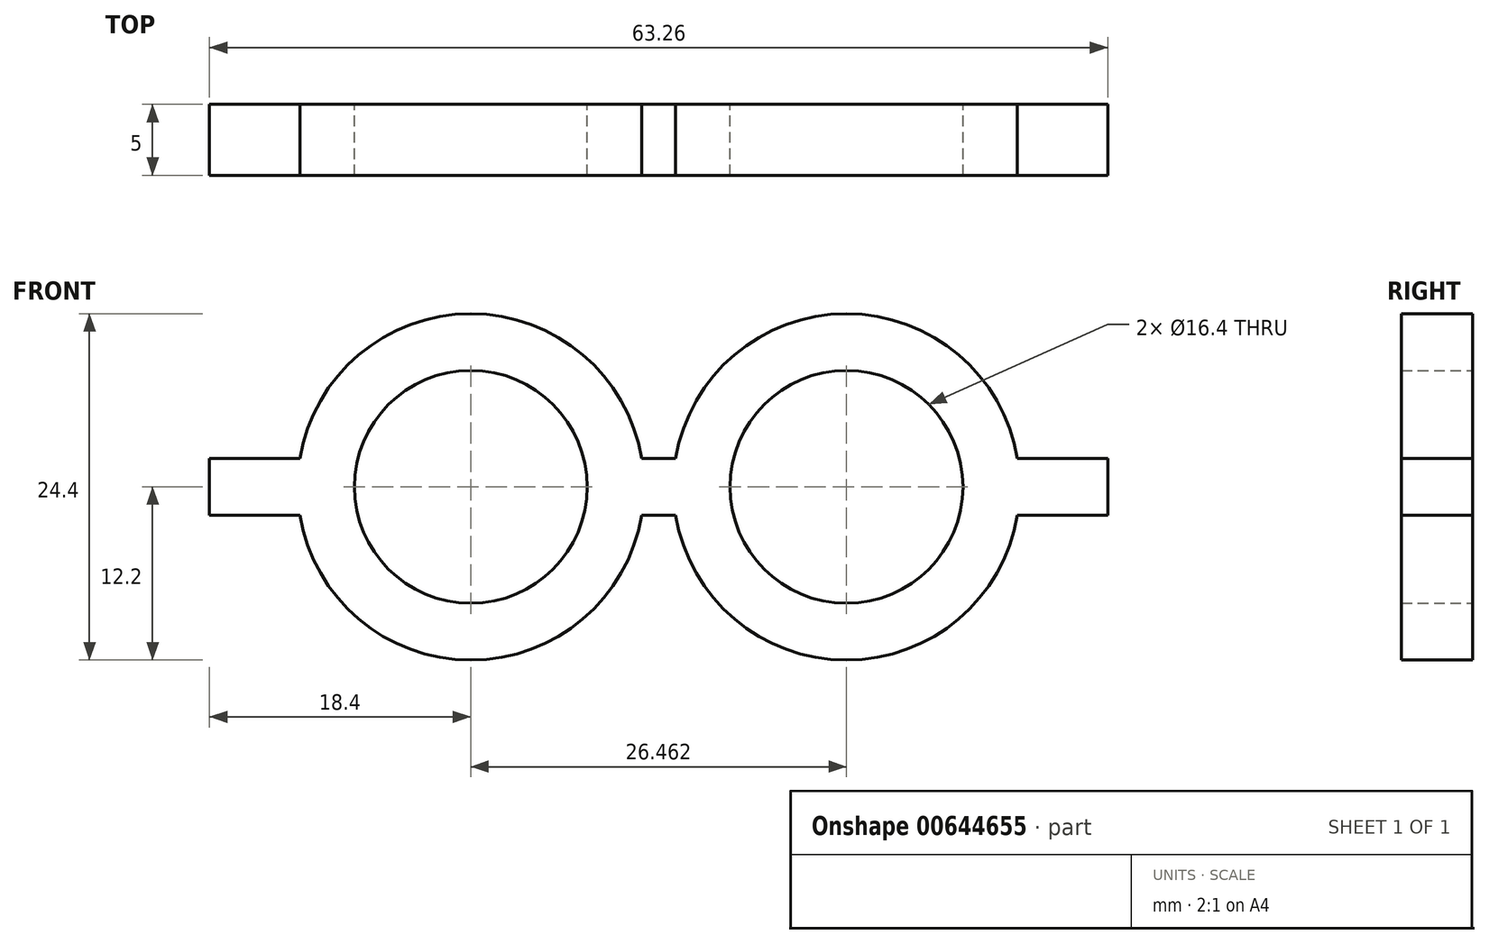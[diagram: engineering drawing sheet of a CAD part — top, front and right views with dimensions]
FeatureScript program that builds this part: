
annotation { "Feature Type Name" : "Feature", "Feature Type Description" : "" }
export const myFeature = defineFeature(function(context is Context, id is Id, definition is map)
    precondition{}
    {
        {
            var Q0;
            Q0=qCreatedBy(makeId("Front.planeOp"),FACE);
            var sketch = newSketch(context, id + "F0", { "sketchPlane" : qUnion([Q0])});
            skCircle(sketch, "E0", {"center": v(0, 0) * mm, "radius": 8.2 * mm});
            skArc(sketch, "E1.0", {"start": v(-12.03, -2) * mm, "mid": v(0, -12.2) * mm, "end": v(12.03, -2) * mm});
            skCircle(sketch, "E2.1.0.0", {"center": v(26.46, 0) * mm, "radius": 8.2 * mm});
            skArc(sketch, "E2.1.0.1", {"start": v(38.5, 2) * mm, "mid": v(26.46, 12.2) * mm, "end": v(14.43, 2) * mm});
            skLineSegment(sketch, "E2.direction1", {"start": v(0, 0) * mm, "end": v(26.46, 0) * mm, "construction": true});
            skLineSegment(sketch, "E3.bottom", {"start": v(14.43, -2) * mm, "end": v(12.03, -2) * mm});
            skLineSegment(sketch, "E3.top", {"start": v(14.43, 2) * mm, "end": v(12.03, 2) * mm});
            skPoint(sketch, "E3.middle", {"position": v(13.23, 0) * mm});
            skLineSegment(sketch, "E4.bottom", {"start": v(44.86, -2) * mm, "end": v(38.5, -2) * mm});
            skLineSegment(sketch, "E4.top", {"start": v(44.86, 2) * mm, "end": v(38.5, 2) * mm});
            skLineSegment(sketch, "E4.left", {"start": v(44.86, -2) * mm, "end": v(44.86, 2) * mm});
            skPoint(sketch, "E4.middle", {"position": v(35.66, 0) * mm});
            skLineSegment(sketch, "E5.right", {"start": v(-18.4, -2) * mm, "end": v(-18.4, 2) * mm});
            skPoint(sketch, "E5.middle", {"position": v(-9.2, 0) * mm});
            skPoint(sketch, "E6.orphan", {"position": v(26.46, 2) * mm});
            skPoint(sketch, "E4.right.start.orphan", {"position": v(26.46, -2) * mm});
            skLineSegment(sketch, "E7.trimOffspring", {"start": v(-12.03, 2) * mm, "end": v(-18.4, 2) * mm});
            skLineSegment(sketch, "E8.trimOffspring", {"start": v(-12.03, -2) * mm, "end": v(-18.4, -2) * mm});
            skPoint(sketch, "E9.orphan", {"position": v(0, 2) * mm});
            skPoint(sketch, "E5.left.start.orphan", {"position": v(0, -2) * mm});
            skArc(sketch, "E10.trimOffspring", {"start": v(12.03, 2) * mm, "mid": v(0, 12.2) * mm, "end": v(-12.03, 2) * mm});
            skArc(sketch, "E11.trimOffspring", {"start": v(14.43, -2) * mm, "mid": v(26.46, -12.2) * mm, "end": v(38.5, -2) * mm});
            skPoint(sketch, "E12.orphan", {"position": v(9.4, -2) * mm});
            skPoint(sketch, "E13.orphan", {"position": v(17.06, -2) * mm});
            skPoint(sketch, "E14.orphan", {"position": v(17.06, 2) * mm});
            skPoint(sketch, "E3.right.end.orphan", {"position": v(9.4, 2) * mm});
            skSolve(sketch);
        }
        {
            var Q0;
            Q0 = qSketchRegion(id + "F0", true);
            extrude(context, id + "F1", {"entities" : qUnion([Q0]), "depth" : 5 * mm, "offsetDistance" : 25 * mm});
        }
    });
